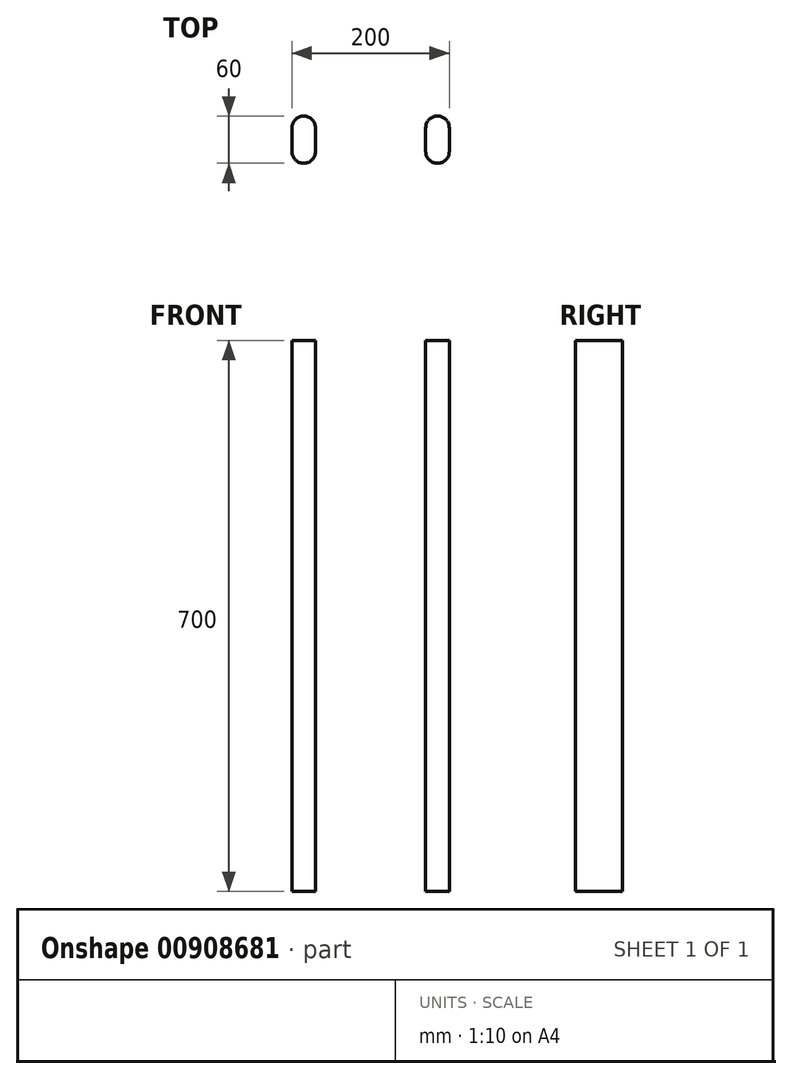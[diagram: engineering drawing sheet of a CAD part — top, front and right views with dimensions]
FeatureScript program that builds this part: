
annotation { "Feature Type Name" : "Feature", "Feature Type Description" : "" }
export const myFeature = defineFeature(function(context is Context, id is Id, definition is map)
    precondition{}
    {
        {
            var Q0;
            Q0=qCreatedBy(makeId("Top.planeOp"),FACE);
            var sketch = newSketch(context, id + "F0", { "sketchPlane" : qUnion([Q0])});
            skLineSegment(sketch, "E0", {"start": v(0, 0) * mm, "end": v(-100, 0) * mm, "construction": true});
            skLineSegment(sketch, "E1.bottom", {"start": v(-85, 0) * mm, "end": v(-85, 0) * mm});
            skLineSegment(sketch, "E1.top", {"start": v(-85, 60) * mm, "end": v(-85, 60) * mm});
            skLineSegment(sketch, "E1.left", {"start": v(-100, 15) * mm, "end": v(-100, 45) * mm});
            skLineSegment(sketch, "E1.right", {"start": v(-70, 15) * mm, "end": v(-70, 45) * mm});
            skLineSegment(sketch, "E2", {"start": v(0, 0) * mm, "end": v(0, 17.15) * mm, "construction": true});
            skPoint(sketch, "E3.visualSharp", {"position": v(-100, 60) * mm});
            skArc(sketch, "E3.filletArc", {"start": v(-85, 60) * mm, "mid": v(-95.6, 55.6) * mm, "end": v(-100, 45) * mm});
            skPoint(sketch, "E4.visualSharp", {"position": v(-70, 60) * mm});
            skArc(sketch, "E4.filletArc", {"start": v(-70, 45) * mm, "mid": v(-74.4, 55.6) * mm, "end": v(-85, 60) * mm});
            skPoint(sketch, "E5.visualSharp", {"position": v(-100, 0) * mm});
            skArc(sketch, "E5.filletArc", {"start": v(-100, 15) * mm, "mid": v(-95.6, 4.4) * mm, "end": v(-85, 0) * mm});
            skPoint(sketch, "E6.visualSharp", {"position": v(-70, 0) * mm});
            skArc(sketch, "E6.filletArc", {"start": v(-85, 0) * mm, "mid": v(-74.4, 4.4) * mm, "end": v(-70, 15) * mm});
            skLineSegment(sketch, "E7.MirrorCS", {"start": v(70, 15) * mm, "end": v(70, 45) * mm});
            skLineSegment(sketch, "E8.MirrorCS", {"start": v(85, 60) * mm, "end": v(85, 60) * mm});
            skArc(sketch, "E9.MirrorCS", {"start": v(70, 45) * mm, "mid": v(74.4, 55.6) * mm, "end": v(85, 60) * mm});
            skArc(sketch, "E10.MirrorCS", {"start": v(85, 0) * mm, "mid": v(74.4, 4.4) * mm, "end": v(70, 15) * mm});
            skPoint(sketch, "E11.MirrorP", {"position": v(100, 0) * mm});
            skLineSegment(sketch, "E12.MirrorCS", {"start": v(100, 15) * mm, "end": v(100, 45) * mm});
            skArc(sketch, "E13.MirrorCS", {"start": v(100, 15) * mm, "mid": v(95.6, 4.4) * mm, "end": v(85, 0) * mm});
            skPoint(sketch, "E14.MirrorP", {"position": v(100, 60) * mm});
            skPoint(sketch, "E15.MirrorP", {"position": v(70, 60) * mm});
            skArc(sketch, "E16.MirrorCS", {"start": v(85, 60) * mm, "mid": v(95.6, 55.6) * mm, "end": v(100, 45) * mm});
            skLineSegment(sketch, "E17.MirrorCS", {"start": v(85, 0) * mm, "end": v(85, 0) * mm});
            skPoint(sketch, "E18.MirrorP", {"position": v(70, 0) * mm});
            skSolve(sketch);
        }
        {
            var Q0;
            Q0=makeQuery(id+"F0.imprint","IMPRINT",FACE,{"disambiguationData":[TD([[makeQuery(id+"F0.imprint","IMPRINT",EDGE,{"derivedFrom":sQuery(id+"F0.wireOp",EDGE,"E1.left")}),-1.0]])]});
            var Q1;
            Q1=makeQuery(id+"F0.imprint","IMPRINT",FACE,{"disambiguationData":[TD([[makeQuery(id+"F0.imprint","IMPRINT",EDGE,{"derivedFrom":sQuery(id+"F0.wireOp",EDGE,"E7.MirrorCS")}),-1.0]])]});
            extrude(context, id + "F1", {"entities" : qUnion([Q0, Q1]), "oppositeDirection" : true, "depth" : 700 * mm, "offsetDistance" : 25 * mm});
        }
    });
